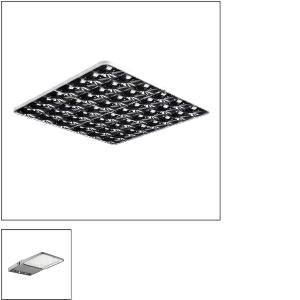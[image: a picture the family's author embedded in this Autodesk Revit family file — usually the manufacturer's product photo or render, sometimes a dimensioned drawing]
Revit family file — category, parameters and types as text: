
# Revit family: siteco_mirrortec_r__indoor___rs05_5nw14091qa_1e52
name_source: partatom
category: Lighting Fixtures
units: mm (PartAtom-declared; Revit-internal decimal feet)

## family parameters
Cut with Voids When Loaded = No
Host = Face
Light Source = No
Part Type = Normal
Room Calculation Point = No
Round Connector Dimension = Use Diameter
Shared = No

## types (1)
- 5XA7682G2H2AC (1 x LED, 34300 lm, 305.7 W, 4000K)
    Apparent Load = 306 VA
    CIE Flux Codes = 47 83 98 49 100
    Color Rendering = 70
    Color Temperature = 4000K
    Default Elevation = 1800 mm
    Description = secondary reflector, for Siteco Mirrortec® Indoor, ball-and-socket joint pendant suspension, housing, square, of aluminium, coated, metallic grey (RAL 9006), fresnel reflector 100, of PMMA, aluminized, highly specular, light point resolution, fresnel structure, length: 600 mm, width: 600 mm

Light Distribution: RS05
    Height = 342 mm
    Lamp = 1 x LED
    Lamp Light Flux = 34300 lm
    Lamp Power = 305.7 W
    Lamp count = 1
    Length = 618 mm
    Luminous efficacy = 112 lm/W
    Manufacturer = Siteco
    ModVariant = No
    Model = 5NW14091QA
    Mounting Place = Ceiling
    Mounting Type = Pendant
    Number of Poles = 1
    OnlyDefault = Yes
    Power Factor = 1
    Product Name = Siteco Mirrortec® Indoor | RS05
    Product group = secondary reflector
    ProductGroupID = 908
    Protection Class = Protection class II
    Protection Degree = IP 66
    RLX_Detail_Level = 1
    RLX_Emergency_Light_Flux = 0 lm
    RLX_Emergency_Type = 0
    RLX_Emergency_Type_DB = No
    RlxData = <blob elided: 104049 chars, md5=eb54526c>
    Socket = socket
    Standby Power = 0 W
    System Light Flux = 34300 lm
    System Power = 306 W
    Type Comments = Floodlight FL 20 midi, floodlight, primary light control with lens, of plastic, primary optical cover: protective disc, of toughened safety glass, transparent, light distribution: RS05, light emission: direct distribution, primary light characteristic: rotationally symmetric, installation type: surface-mounted, LED, High Power LED, rated luminous flux: 38.380lm, luminous efficacy: 126lm/W, light colour: 740, colour temperature: 4000K, control gear: ECG Plus, control: overheat protection, power reduction, digital communication interface, time-dependent luminous flux control, flexible luminous flux parameterisation, electronic power reduction, with terminal, 10-pole, max. 2.5mm², mains connection: 220..240V, AC, 50/60Hz, rated input power: 306W, LED unit, of diecast aluminium, powder-coated, Siteco® metallic grey (DB 702S), corrosivity category C5 mid according to DIN EN ISO 12944, length: 731mm, width: 450mm, height: 76mm, housing frame, of diecast aluminium, powder-coated, Siteco® metallic grey (DB 702S), wall fastening, DALI, protection rating (complete): IP66, insulation class (complete): insulation class II (safety insulation), certification: CE, ENEC, VDE, protection symbol: D, permissible operating ambient temperature: -40..+40°C, permissible operating ambient temperature for outdoor applications: -40..+50°C, standard: DIN EN 12944, packaging unit: 1 piece

individual setting: distance floodlight mirror = 2,0m / reflector tilt = 5°
    Type Image = l_577132_1005944.jpg
    URL = http://relux.com
    VarID = 5xa7682g2h2ac@adj_153001
    Voltage = 0 V
    Weight = 0.00 kg
    Width = 618 mm

## geometry (parser evidence)
native form markers: Blend x4, Sweep x8
no freeform markers — native parametric forms only
